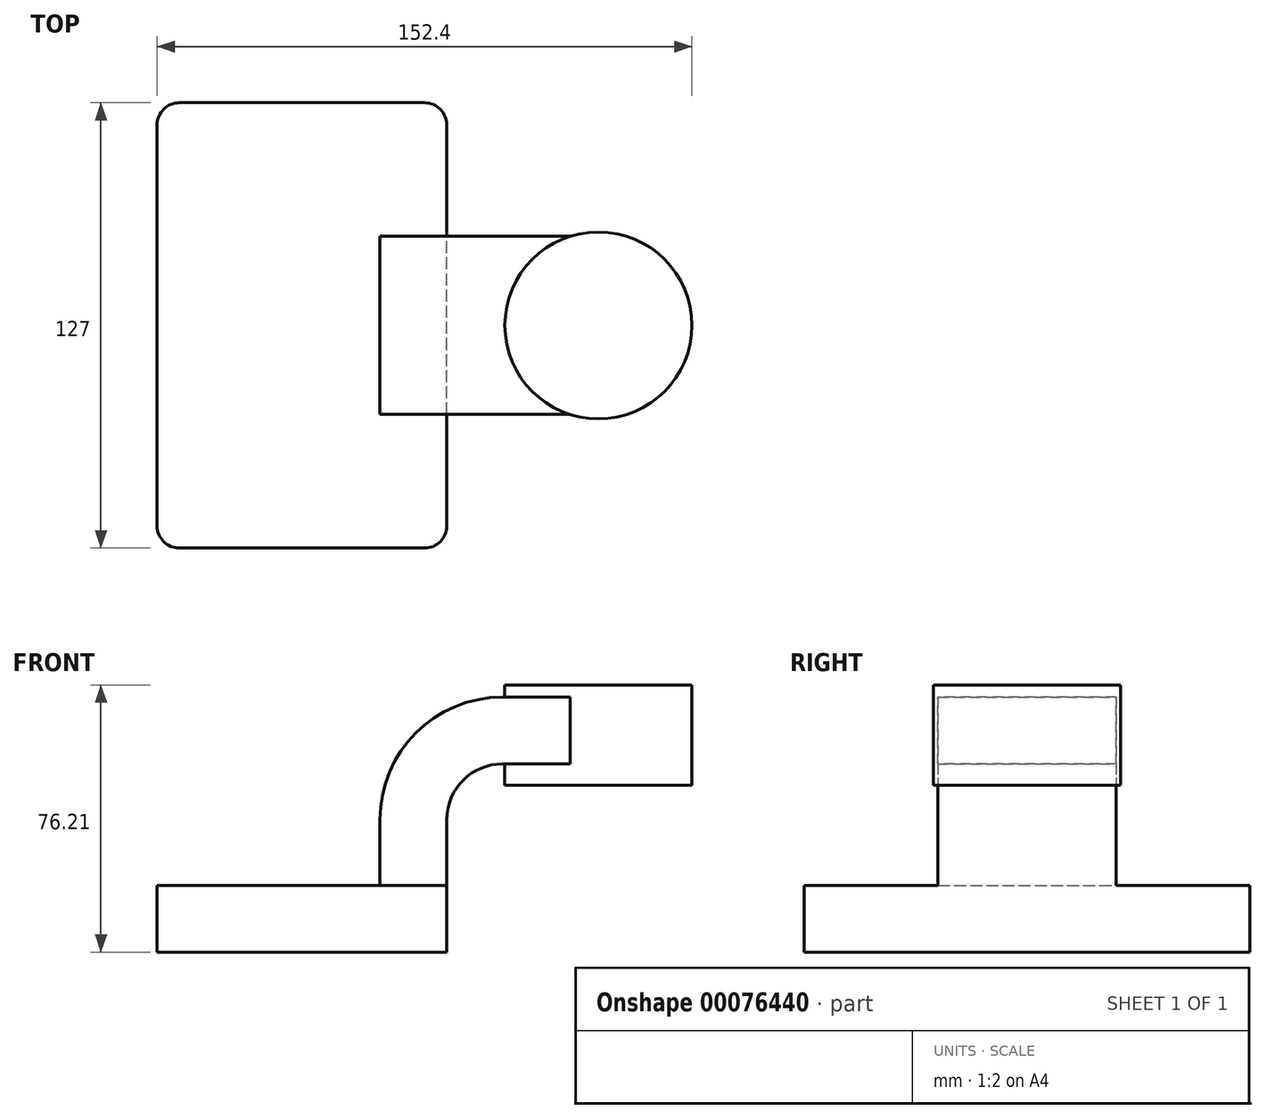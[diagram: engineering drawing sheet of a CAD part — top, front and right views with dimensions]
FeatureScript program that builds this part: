
annotation { "Feature Type Name" : "Feature", "Feature Type Description" : "" }
export const myFeature = defineFeature(function(context is Context, id is Id, definition is map)
    precondition{}
    {
        {
            var Q0;
            Q0=qCreatedBy(makeId("Front.planeOp"),FACE);
            var sketch = newSketch(context, id + "F0", { "sketchPlane" : qUnion([Q0])});
            skLineSegment(sketch, "E0.bottom", {"start": v(-41.28, -9.53) * mm, "end": v(41.28, -9.53) * mm});
            skLineSegment(sketch, "E0.top", {"start": v(-41.28, 9.53) * mm, "end": v(41.28, 9.53) * mm});
            skLineSegment(sketch, "E0.left", {"start": v(-41.28, -9.53) * mm, "end": v(-41.28, 9.53) * mm});
            skLineSegment(sketch, "E0.right", {"start": v(41.28, -9.53) * mm, "end": v(41.28, 9.53) * mm});
            skPoint(sketch, "E0.middle", {"position": v(0, 0) * mm});
            skLineSegment(sketch, "E1.bottom", {"start": v(60.32, 66.68) * mm, "end": v(111.12, 66.68) * mm});
            skLineSegment(sketch, "E1.top", {"start": v(60.32, 38.1) * mm, "end": v(111.12, 38.1) * mm});
            skLineSegment(sketch, "E1.left", {"start": v(60.32, 66.67) * mm, "end": v(60.32, 38.1) * mm});
            skLineSegment(sketch, "E1.right", {"start": v(111.12, 66.68) * mm, "end": v(111.12, 38.1) * mm});
            skPoint(sketch, "E1.middle", {"position": v(85.72, 52.39) * mm});
            skLineSegment(sketch, "E2", {"start": v(41.28, 9.53) * mm, "end": v(41.28, 28.27) * mm});
            skArc(sketch, "E3", {"start": v(41.27, 28.27) * mm, "mid": v(45.92, 39.5) * mm, "end": v(57.15, 44.15) * mm});
            skLineSegment(sketch, "E4", {"start": v(57.15, 44.15) * mm, "end": v(84.47, 44.15) * mm});
            skLineSegment(sketch, "E5.0", {"start": v(57.15, 63.2) * mm, "end": v(84.47, 63.2) * mm});
            skArc(sketch, "E5.1", {"start": v(22.23, 28.27) * mm, "mid": v(32.45, 52.97) * mm, "end": v(57.15, 63.2) * mm});
            skLineSegment(sketch, "E5.2", {"start": v(22.22, 9.53) * mm, "end": v(22.22, 28.27) * mm});
            skLineSegment(sketch, "E6", {"start": v(84.47, 66.68) * mm, "end": v(84.47, 38.1) * mm});
            skFitSpline(sketch, "E7", {"points": [v(57.15, 63.2) * mm, v(-41.28, 9.53) * mm], "startDerivative": vector(-132.82, 7.77) * mm, "endDerivative": vector(2.1, -87.89) * mm});
            skSolve(sketch);
        }
        {
            var Q0;
            Q0=makeQuery(id+"F0.imprint","IMPRINT",FACE,{"disambiguationData":[TD([[makeQuery(id+"F0.imprint","IMPRINT",EDGE,{"derivedFrom":sQuery(id+"F0.wireOp",EDGE,"E0.bottom")}),1.0]])]});
            extrude(context, id + "F1", {"entities" : qUnion([Q0]), "endBound" : BoundingType.SYMMETRIC, "depth" : 127 * mm});
        }
        {
            var Q0;
            {var subQ1=sQuery(id+"F0.wireOp",EDGE,"E2");Q0=makeQuery(id+"F0.imprint","IMPRINT",FACE,{"disambiguationData":[TD([[makeQuery(id+"F0.imprint","IMPRINT",EDGE,{"derivedFrom":subQ1}),1.0]])]});}
            extrude(context, id + "F2", {"entities" : qUnion([Q0]), "operationType" : NewBodyOperationType.ADD, "endBound" : BoundingType.SYMMETRIC, "depth" : 50.8 * mm});
        }
        {
            var Q0;
            Q0=makeQuery(id+"F0.imprint","IMPRINT",FACE,{"disambiguationData":[TD([[makeQuery(id+"F0.imprint","IMPRINT",EDGE,{"derivedFrom":sQuery(id+"F0.wireOp",EDGE,"E5.1")}),1.0]])]});
            extrude(context, id + "F3", {"entities" : qUnion([Q0]), "operationType" : NewBodyOperationType.ADD, "endBound" : BoundingType.SYMMETRIC, "depth" : 15.88 * mm});
        }
        {
            var Q0;
            {var subQ0=sQuery(id+"F0.wireOp",EDGE,"E5.0");var subQ1=sQuery(id+"F0.wireOp",EDGE,"E1.left");var subQ2=makeQuery(id+"F0.imprint","INTERSECT",VERTEX,{"derivedFrom":[subQ1,subQ0]});Q0=makeQuery(id+"F0.imprint","IMPRINT",FACE,{"disambiguationData":[TD([[makeQuery(id+"F0.imprint","IMPRINT",EDGE,{"disambiguationData":[TD([[subQ2,-1.0]])],"derivedFrom":subQ1}),1.0]])]});}
            extrude(context, id + "F4", {"entities" : qUnion([Q0]), "operationType" : NewBodyOperationType.ADD, "endBound" : BoundingType.SYMMETRIC, "depth" : 50.8 * mm});
        }
        {
            var Q0;
            {var subQ0=sQuery(id+"F0.wireOp",EDGE,"E1.right");Q0=makeQuery(id+"F0.imprint","IMPRINT",FACE,{"disambiguationData":[TD([[makeQuery(id+"F0.imprint","IMPRINT",EDGE,{"derivedFrom":subQ0}),-1.0]])]});}
            var Q1;
            Q1=sQuery(id+"F0.wireOp",EDGE,"E6");
            revolve(context, id + "F5", {"operationType" : NewBodyOperationType.ADD, "entities" : qUnion([Q0]), "axis" : qUnion([Q1]), "revolveType" : RevolveType.FULL});
        }
        {
            var Q0;
            Q0=makeQuery(id+"F1.opExtrude","CAP_EDGE",EDGE,{"disambiguationData":[OSD([sQuery(id+"F0.wireOp",EDGE,"E0.left")])],"isStart":false});
            var Q1;
            Q1=makeQuery(id+"F1.opExtrude","CAP_EDGE",EDGE,{"disambiguationData":[OSD([sQuery(id+"F0.wireOp",EDGE,"E0.right")])],"isStart":false});
            var Q2;
            Q2=makeQuery(id+"F1.opExtrude","CAP_EDGE",EDGE,{"disambiguationData":[OSD([sQuery(id+"F0.wireOp",EDGE,"E0.left")])],"isStart":true});
            var Q3;
            Q3=makeQuery(id+"F1.opExtrude","CAP_EDGE",EDGE,{"disambiguationData":[OSD([sQuery(id+"F0.wireOp",EDGE,"E0.right")])],"isStart":true});
            fillet(context, id + "F6", {"entities" : qUnion([Q0, Q1, Q2, Q3]), "radius" : 6.35 * mm, "tangentPropagation" : true, "allowEdgeOverflow" : false});
        }
    });
